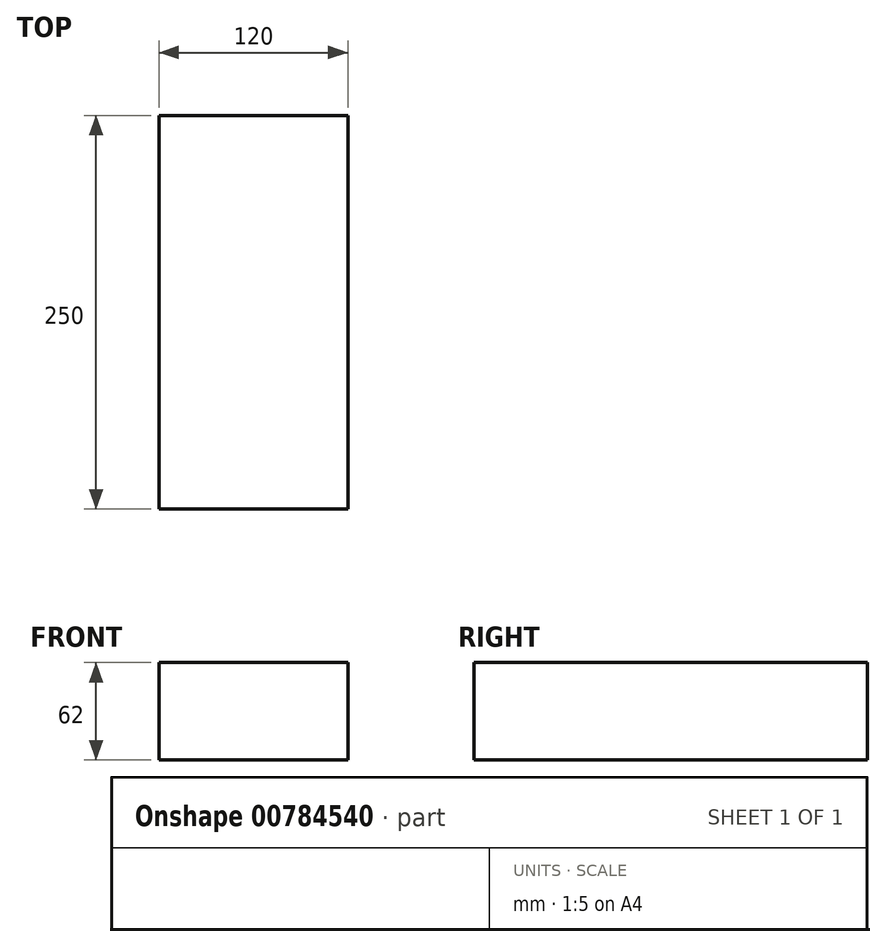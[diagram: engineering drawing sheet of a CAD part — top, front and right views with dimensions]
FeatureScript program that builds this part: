
annotation { "Feature Type Name" : "Feature", "Feature Type Description" : "" }
export const myFeature = defineFeature(function(context is Context, id is Id, definition is map)
    precondition{}
    {
        {
            var Q0;
            Q0=qCreatedBy(makeId("Front.planeOp"),FACE);
            var sketch = newSketch(context, id + "F0", { "sketchPlane" : qUnion([Q0])});
            skLineSegment(sketch, "E0.bottom", {"start": v(0, 0) * mm, "end": v(120, 0) * mm});
            skLineSegment(sketch, "E0.top", {"start": v(0, 62) * mm, "end": v(120, 62) * mm});
            skLineSegment(sketch, "E0.left", {"start": v(0, 0) * mm, "end": v(0, 62) * mm});
            skLineSegment(sketch, "E0.right", {"start": v(120, 0) * mm, "end": v(120, 62) * mm});
            skSolve(sketch);
        }
        {
            var Q0;
            Q0=makeQuery(id+"F0.imprint","IMPRINT",FACE,{"disambiguationData":[TD([[makeQuery(id+"F0.imprint","IMPRINT",EDGE,{"derivedFrom":sQuery(id+"F0.wireOp",EDGE,"E0.bottom")}),1.0]])]});
            extrude(context, id + "F1", {"entities" : qUnion([Q0]), "depth" : 250 * mm, "offsetDistance" : 25 * mm});
        }
    });
